# Revit family: Haworth_Compose_Panel_Benching
name_source: partatom
category: Furniture Systems
revit_build: Autodesk Revit 2018 (Build: 20170223_1515(x64)
units: mm (PartAtom-declared; Revit-internal decimal feet)

## family parameters
Always vertical = Yes
Cut with Voids When Loaded = No
OmniClass Number = 23.40.70.14.64.21
OmniClass Title = Systems Furniture
Part Type = Normal
Room Calculation Point = No
Round Connector Dimension = Use Diameter
Shared = No
Work Plane-Based = No

## types (18) — shared parameters
Actual Height = 28 7/8"
Assembly Code = E2020500
Bottom Trim Width = 1 1/2"
Custom Size = No
Description = Haworth_Compose-Panel-Benching
Manufacturer = Haworth
Max. Height = 30"
Max. Width = 72"
Min. Height = 22"
Min. Width = 18"
Min/Max Width = 18, 24, 30, 36, 42, 48, 54, 60, 72
Model = VZFF
Panel Depth = 1/2"
Raceway Finish = Haworth _ Paint _ Putty
Raceway Panel Depth = 1/2"
Revision Number = 4
Size = Verify Final Dim. w/ Haworth
Sustainability Info = http://media.haworth.com
Top Trim = Yes
Top Trim Adjuster = 1/8"
Top Trim Width = 1/8"
Trim Depth = 3"
Trim Finish = Haworth _ Paint _ Putty
Trim Thin Profile = Yes
URL = http://www.haworth.com
URL - Product = http://www.haworth.com
Vertical Trim Width = 1/4"
Warranty = http://www.haworth.com

## per-type parameters (varying)
| type | Actual Width | Panel Width | Raceway Back Panel | Raceway Front Panel | Raceway Panel Width | Width |
| 29h 18w - Tile to the Floor | 18" | 18" | No | No | 18" | 18" |
| 29h 24w - Tile to the Floor | 24" | 24" | No | No | 24" | 24" |
| 29h 30w - Tile to the Floor | 30" | 30" | No | No | 30" | 30" |
| 29h 36w - Tile to the Floor | 36" | 36" | No | No | 36" | 36" |
| 29h 42w - Tile to the Floor | 42" | 42" | No | No | 42" | 42" |
| 29h 48w - Tile to the Floor | 48" | 48" | No | No | 48" | 48" |
| 29h 54w - Tile to the Floor | 54" | 54" | No | No | 54" | 54" |
| 29h 60w - Tile to the Floor | 60" | 60" | No | No | 60" | 60" |
| 29h 72w - Tile to the Floor | 72" | 72" | No | No | 72" | 72" |
| 29h 18w - Base Raceway | 18" | 18" | Yes | Yes | 18" | 18" |
| 29h 24w - Base Raceway | 24" | 24" | Yes | Yes | 24" | 24" |
| 29h 30w - Base Raceway | 30" | 30" | Yes | Yes | 30" | 30" |
| 29h 36w - Base Raceway | 36" | 36" | Yes | Yes | 36" | 36" |
| 29h 42w - Base Raceway | 42" | 42" | Yes | Yes | 42" | 42" |
| 29h 48w - Base Raceway | 48" | 48" | Yes | Yes | 48" | 48" |
| 29h 54w - Base Raceway | 54" | 54" | Yes | Yes | 54" | 54" |
| 29h 60w - Base Raceway | 60" | 60" | Yes | Yes | 60" | 60" |
| 29h 72w - Base Raceway | 72" | 72" | Yes | Yes | 72" | 72" |

## geometry (parser evidence)
native form markers: Sweep x12
no freeform markers — native parametric forms only
